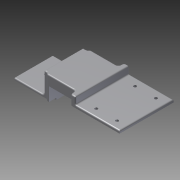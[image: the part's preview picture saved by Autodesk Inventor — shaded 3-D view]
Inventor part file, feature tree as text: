
AUTODESK INVENTOR PART (.ipt)
format: ipt  version: 2012 (Build 160160000, 160)  size: 491,008 bytes
history: native  units: mm
features: extrude x23, sketch x23, projected_geometry x18, reference x11, plane x10, fillet x7, other x1
ambient origin geometry x8: Origin, YZ Plane, XZ Plane, XY Plane, X Axis, Y Axis, Z Axis, Center Point
feature tree (93):
  plane  "Work Plane4"
  extrude  "Extrusion7"  Depth=2.0mm
  plane  "Work Plane5"
  sketch  "Sketch9"  dims[d40=20.0mm d41=0.0mm d42=20.0mm d43=0.0mm]
  plane  "Work Plane6"
  extrude  "Extrusion8"  Depth=20.0mm TaperAngle=0.0deg
  sketch  "Sketch10"  dims[d44=20.0mm d45=0.0mm d46=20.0mm d47=0.0mm]
  plane  "Work Plane7"
  extrude  "Extrusion9"  Depth=20.0mm TaperAngle=0.0deg
  extrude  "Extrusion10"  Depth=20.0mm TaperAngle=0.0deg
  sketch  "Sketch12"  dims[d52=2.0mm d53=0.0mm d54=2.0mm d55=0.0mm]
  plane  "Work Plane8"
  extrude  "Extrusion11"  Depth=2.0mm TaperAngle=0.0deg
  sketch  "Sketch13"  dims[d56=0.3mm d57=0.3mm d58=0.3mm]
  plane  "Work Plane9"
  extrude  "Extrusion12"  Depth=0.3mm
  extrude  "Extrusion13"  Depth=0.3mm
  sketch  "Sketch15"  dims[d62=0.3mm d70=10.0mm d71=0.0mm]
  plane  "Work Plane10"
  extrude  "Extrusion14"  Depth=10.0mm TaperAngle=0.0deg
  plane  "Work Plane11"
  plane  "Work Plane12"
  extrude  "Extrusion17"  Depth=10.0mm TaperAngle=0.0deg
  extrude  "Extrusion18"  Depth=3.75mm
  extrude  "Extrusion19"  Depth=2.5mm
  extrude  "Extrusion20"  Depth=9.0mm
  sketch  "Sketch24"  dims[d87=2.0mm d88=0.0mm]
  plane  "Work Plane13"
  extrude  "Extrusion21"  TaperAngle=0.0deg  [1 undecoded]
  extrude  "Extrusion22"  Depth=9.0mm
  other  "Work Axis1"
  extrude  "Extrusion23"  Depth=4.5mm
  extrude  "Extrusion24"  Depth=0.3mm
  extrude  "Extrusion25"  Depth=0.3mm
  extrude  "Extrusion26"  Depth=25.0mm TaperAngle=0.0deg
  extrude  "Extrusion27"  Depth=2.0mm
  fillet  "Fillet17"  Radius=9.4mm
  fillet  "Fillet18"  Radius=16.76mm
  fillet  "Fillet19"  Radius=33.6mm
  extrude  "Extrusion28"  Depth=9.0mm
  extrude  "Extrusion29"  Depth=4.7mm
  extrude  "Extrusion30"  Depth=10.0mm TaperAngle=0.0deg
  extrude  "Extrusion31"  Depth=0.6mm TaperAngle=0.0deg
  fillet  "Fillet20"  Radius=0.3mm
  fillet  "Fillet21"  Radius=0.3mm
  fillet  "Fillet22"  Radius=0.3mm
  fillet  "Fillet23"  Radius=2.0mm
  sketch  "Sketch8"  dims[d38=2.0mm d39=2.0mm]
  reference  "Reference5"
  reference  "Reference6"
  reference  "Reference7"
  reference  "Reference8"
  projected_geometry  "Projected Loop11"
  reference  "Reference9"
  reference  "Reference10"
  projected_geometry  "Projected Loop12"
  sketch  "Sketch11"  dims[d48=20.0mm d49=0.0mm d50=20.0mm d51=0.0mm]
  projected_geometry  "Projected Loop13"
  reference  "Reference11"
  projected_geometry  "Projected Loop14"
  projected_geometry  "Projected Loop15"
  sketch  "Sketch14"  dims[d60=0.3mm d61=0.3mm]
  projected_geometry  "Projected Loop16"
  projected_geometry  "Projected Loop17"
  sketch  "Sketch19"  dims[d73=2.5mm d74=10.0mm d75=0.0mm]
  sketch  "Sketch20"  dims[d77=7.5mm d79=3.75mm]
  projected_geometry  "Projected Loop23"
  sketch  "Sketch21"  dims[d81=3.75mm d82=2.5mm]
  projected_geometry  "Projected Loop24"
  reference  "Reference19"
  sketch  "Sketch23"  dims[d83=10.0mm d84=0.0mm d86=9.0mm]
  projected_geometry  "Projected Loop25"
  sketch  "Sketch26"  dims[d89=4.5mm d90=9.0mm]
  projected_geometry  "Projected Loop26"
  sketch  "Sketch27"  dims[d91=2.0mm d92=4.5mm]
  projected_geometry  "Projected Loop27"
  sketch  "Sketch28"  dims[d103=0.3mm d104=0.3mm]
  projected_geometry  "Projected Loop28"
  sketch  "Sketch29"  dims[d105=0.3mm d106=0.3mm]
  projected_geometry  "Projected Loop29"
  sketch  "Sketch30"  dims[d107=10.0mm d108=0.0mm d110=25.0mm d111=0.0mm]
  projected_geometry  "Projected Loop30"
  sketch  "Sketch32"  dims[d112=0.3mm d113=2.0mm d114=9.4mm d115=16.76mm d116=33.6mm]
  projected_geometry  "Projected Loop31"
  sketch  "Sketch33"  dims[d117=8.42mm d118=9.0mm]
  projected_geometry  "Projected Loop32"
  sketch  "Sketch34"  dims[d119=8.38mm d120=4.7mm]
  projected_geometry  "Projected Loop33"
  sketch  "Sketch35"  dims[d121=4.0mm d122=10.0mm d123=0.0mm]
  sketch  "Sketch36"  dims[d124=0.3mm d125=0.0mm d126=0.6mm d127=0.0mm d128=0.3mm d129=0.0mm d130=0.3mm d131=0.0mm d132=0.3mm d133=0.0mm d138=2.0mm d139=1.0mm d140=1.0mm d141=10.0mm d142=0.0mm d143=2.0mm d144=0.0mm d145=30.5mm d146=8.5mm d147=0.0mm d148=0.0mm d149=30.5mm d150=0.0mm d151=2.0mm d152=2.0mm d153=1.0mm d154=1.0mm d155=2.5mm d156=23.25mm d157=11.625mm d158=11.625mm d159=4.5mm d160=4.5mm d161=2.5mm d162=4.5mm d163=2.5mm]
  reference  "Reference21"
  reference  "Reference22"
  reference  "Reference23"
note: 1 required parameter value undecoded (feature->parameter linkage not recoverable at this tier; creation-order binding heuristic only, values carry confidence <= 0.55)
